# Revit family: SQI-D
name_source: partatom
category: Mechanical Equipment
units: mm (PartAtom-declared; Revit-internal decimal feet)

## family parameters
Always vertical = Yes
Cut with Voids When Loaded = No
Part Type = Normal
Room Calculation Point = No
Round Connector Dimension = Use Diameter
Shared = No
Work Plane-Based = No

## types (7) — shared parameters
0 = 0"
1" = 1"
1.5 = 1 1/2"
2" = 2"
2' = 24"
3" = 3"
4" = 4"
E = 14 5/16"
E/2 = 7 5/32"
Manufacturer = Loren Cook Company
Model = SQI-HP
ONE EIGTH = 1/8"
Type Comments = Square Centrifugal High Pressure Inline Belt Drive
URL = www.lorencook.com

## per-type parameters (varying)
| type | (A+.25")/2 | -C/2 | A | A+.25" | A/2 | B | B/2 | C | C-.125" | C/2 | D | D/2 | D/3 | D/6 | MOTOR_DEPTH |
| 90_SQI-D | 7 11/32" | -8 13/32" | 14 7/16" | 14 11/16" | 7 7/32" | 14 3/8" | 7 3/16" | 16 13/16" | 16 11/16" | 8 13/32" | 17 1/2" | 8 3/4" | 5 27/32" | 2 29/32" | -16" |
| 120_SQI-D | 8 13/16" | -10 3/32" | 17 3/8" | 17 5/8" | 8 11/16" | 17 3/4" | 8 7/8" | 20 3/16" | 20 1/16" | 10 3/32" | 20 1/2" | 10 1/4" | 6 27/32" | 3 13/32" | -18" |
| 135_SQI-D | 9 7/8" | -11 11/32" | 19 1/2" | 19 3/4" | 9 3/4" | 20 1/4" | 10 1/8" | 22 11/16" | 22 9/16" | 11 11/32" | 22 5/8" | 11 5/16" | 7 17/32" | 3 25/32" | -18" |
| 150_SQI-D | 10 15/16" | -12 5/8" | 21 5/8" | 21 7/8" | 10 13/16" | 22 13/16" | 11 13/32" | 25 1/4" | 25 1/8" | 12 5/8" | 24 3/4" | 12 3/8" | 8 1/4" | 4 1/8" | -18" |
| 165_SQI-D | 12 1/32" | -13 7/8" | 23 13/16" | 24 1/16" | 11 29/32" | 25 5/16" | 12 21/32" | 27 3/4" | 27 5/8" | 13 7/8" | 26 15/16" | 13 15/32" | 8 31/32" | 4 1/2" | -20" |
| 70_SQI-D | 5 3/16" | -5 7/8" | 10 1/8" | 10 3/8" | 5 1/16" | 9 3/4" | 4 7/8" | 11 3/4" | 11 5/8" | 5 7/8" | 13 1/8" | 6 9/16" | 4 3/8" | 2 3/16" | -16" |
| 80_SQI-D | 6 5/8" | -7 9/16" | 13" | 13 1/4" | 6 1/2" | 13" | 6 1/2" | 15 1/8" | 15" | 7 9/16" | 16" | 8" | 5 11/32" | 2 21/32" | -16" |

## geometry (parser evidence)
native form markers: Sweep x2
no freeform markers — native parametric forms only
